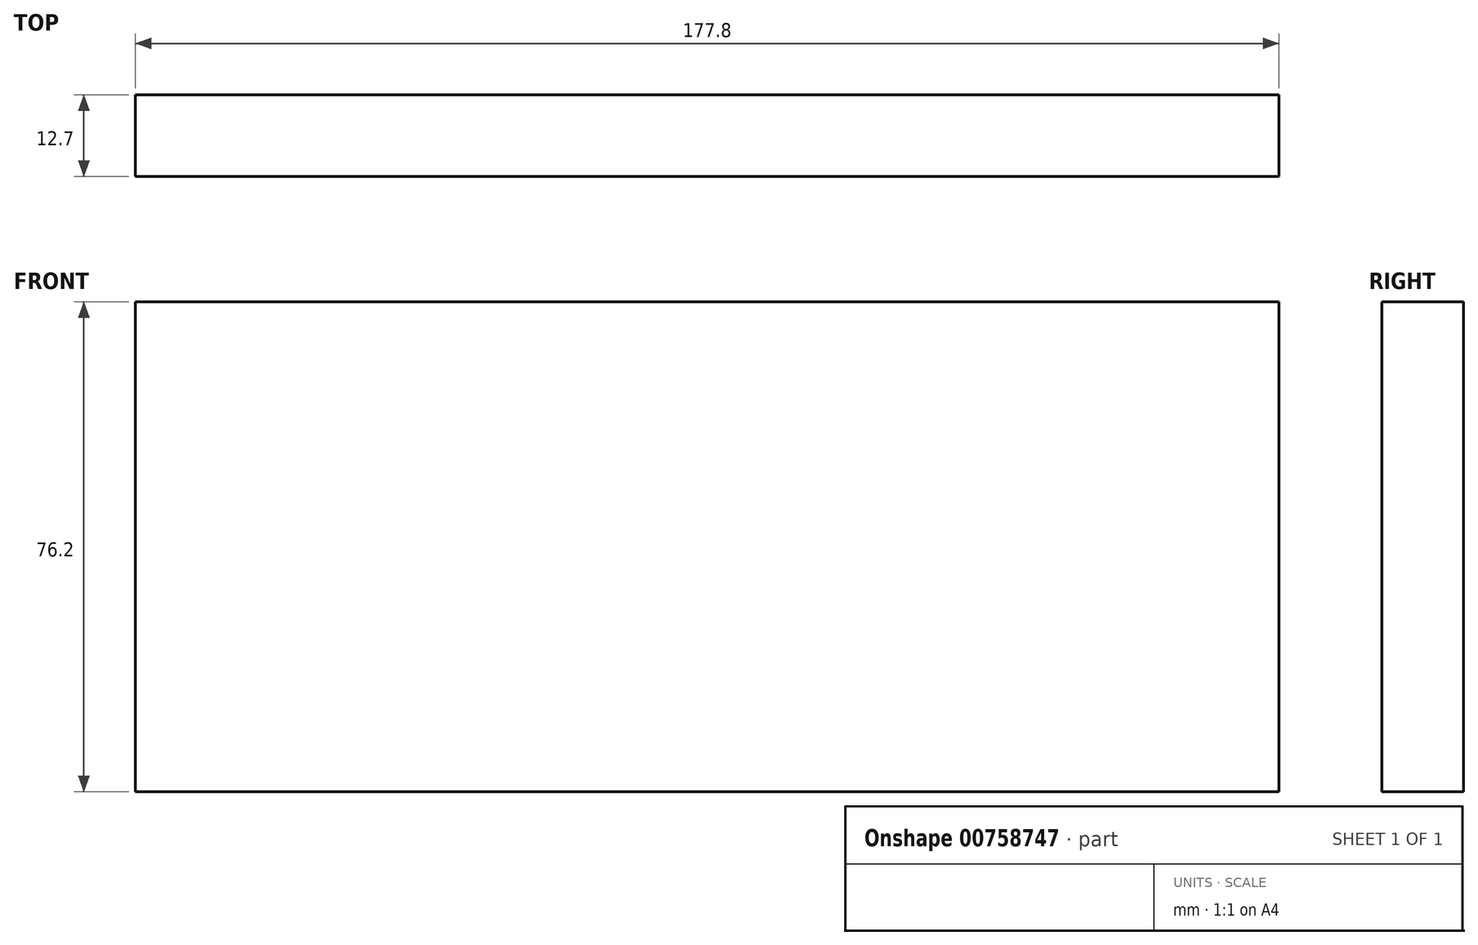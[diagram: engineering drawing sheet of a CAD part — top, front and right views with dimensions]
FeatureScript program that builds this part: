
annotation { "Feature Type Name" : "Feature", "Feature Type Description" : "" }
export const myFeature = defineFeature(function(context is Context, id is Id, definition is map)
    precondition{}
    {
        {
            var Q0;
            Q0=qCreatedBy(makeId("Front.planeOp"),FACE);
            var sketch = newSketch(context, id + "F0", { "sketchPlane" : qUnion([Q0])});
            skLineSegment(sketch, "E0.bottom", {"start": v(-85.58, 81.83) * mm, "end": v(92.22, 81.83) * mm});
            skLineSegment(sketch, "E0.top", {"start": v(-85.58, 5.63) * mm, "end": v(92.22, 5.63) * mm});
            skLineSegment(sketch, "E0.left", {"start": v(-85.58, 81.83) * mm, "end": v(-85.58, 5.63) * mm});
            skLineSegment(sketch, "E0.right", {"start": v(92.22, 81.83) * mm, "end": v(92.22, 5.63) * mm});
            skLineSegment(sketch, "E1.left", {"start": v(-85.58, 81.83) * mm, "end": v(-85.58, 81.83) * mm});
            skLineSegment(sketch, "E1.right", {"start": v(92.22, 81.83) * mm, "end": v(92.22, 81.83) * mm});
            skSolve(sketch);
        }
        {
            var Q0;
            Q0=makeQuery(id+"F0.imprint","IMPRINT",FACE,{"disambiguationData":[TD([[makeQuery(id+"F0.imprint","IMPRINT",EDGE,{"derivedFrom":sQuery(id+"F0.wireOp",EDGE,"E0.top")}),1.0]])]});
            extrude(context, id + "F1", {"entities" : qUnion([Q0]), "depth" : 12.7 * mm, "offsetDistance" : 25.4 * mm});
        }
    });
